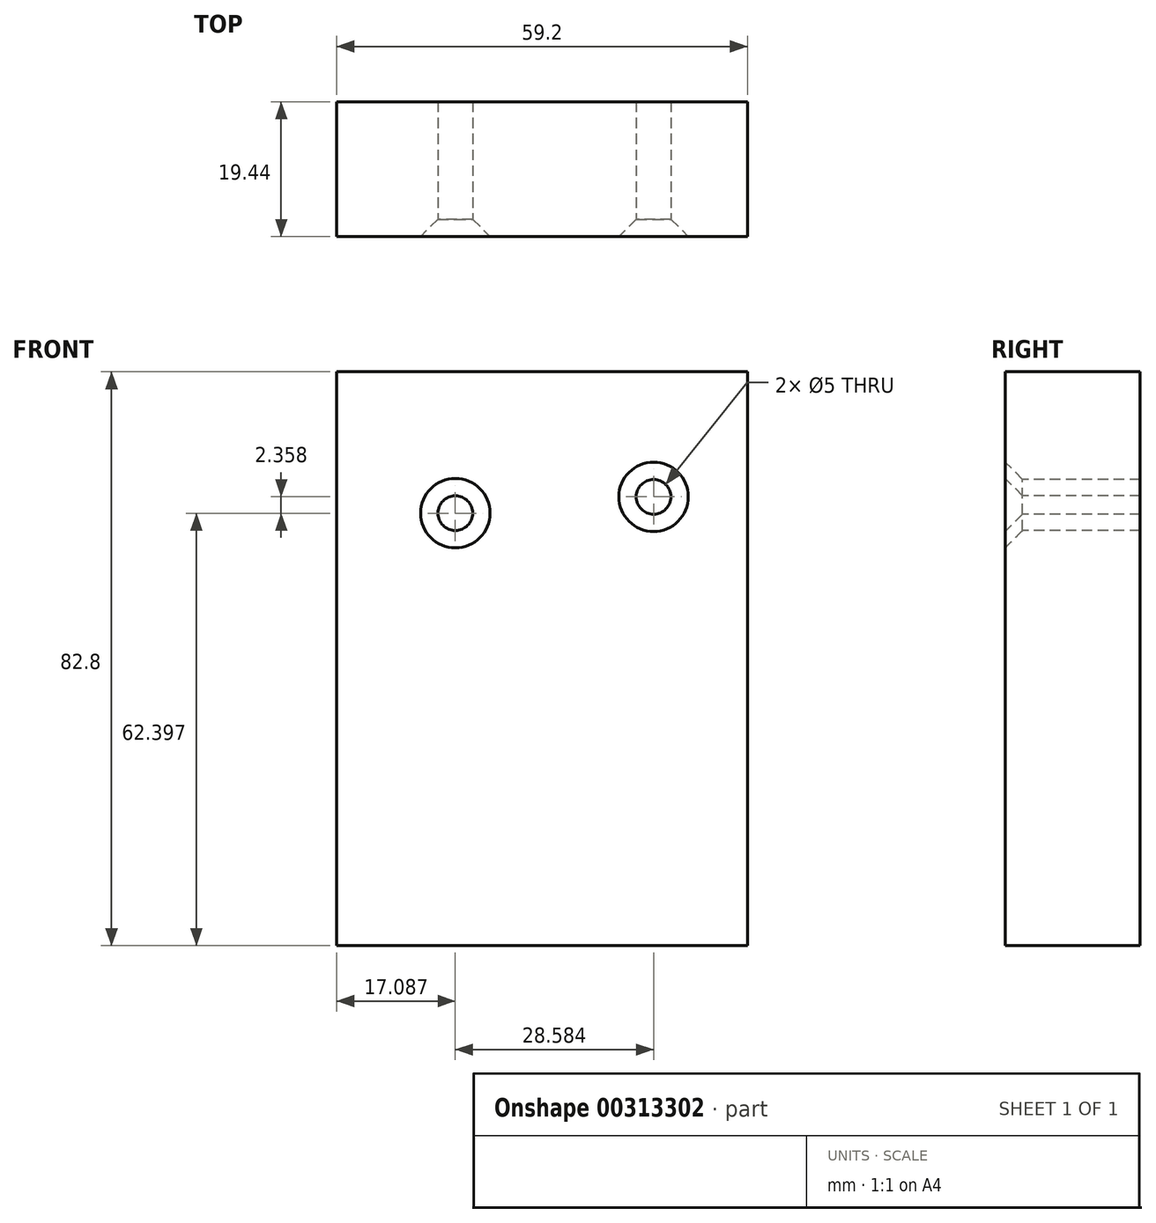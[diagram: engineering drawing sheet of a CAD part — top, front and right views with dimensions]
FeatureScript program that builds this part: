
annotation { "Feature Type Name" : "Feature", "Feature Type Description" : "" }
export const myFeature = defineFeature(function(context is Context, id is Id, definition is map)
    precondition{}
    {
        {
            var Q0;
            Q0=qCreatedBy(makeId("Top.planeOp"),FACE);
            var sketch = newSketch(context, id + "F0", { "sketchPlane" : qUnion([Q0])});
            skLineSegment(sketch, "E0.bottom", {"start": v(-35.02, -10.8) * mm, "end": v(24.18, -10.8) * mm});
            skLineSegment(sketch, "E0.top", {"start": v(-35.02, 8.65) * mm, "end": v(24.18, 8.65) * mm});
            skLineSegment(sketch, "E0.left", {"start": v(-35.02, -10.8) * mm, "end": v(-35.02, 8.65) * mm});
            skLineSegment(sketch, "E0.right", {"start": v(24.18, -10.8) * mm, "end": v(24.18, 8.65) * mm});
            skSolve(sketch);
        }
        {
            var Q0;
            Q0=makeQuery(id+"F0.imprint","IMPRINT",FACE,{"disambiguationData":[TD([[makeQuery(id+"F0.imprint","IMPRINT",EDGE,{"derivedFrom":sQuery(id+"F0.wireOp",EDGE,"E0.bottom")}),1.0]])]});
            extrude(context, id + "F1", {"entities" : qUnion([Q0]), "depth" : 82.8 * mm});
        }
        {
            var Q0;
            Q0=makeQuery(id+"F1.opExtrude","SWEPT_FACE",FACE,{"disambiguationData":[OSD([sQuery(id+"F0.wireOp",EDGE,"E0.bottom")])]});
            var sketch = newSketch(context, id + "F2", { "sketchPlane" : qUnion([Q0])});
            skPoint(sketch, "E1", {"position": v(-17.93, 62.4) * mm});
            skPoint(sketch, "E2", {"position": v(10.65, 64.75) * mm});
            skSolve(sketch);
        }
        {
            var Q0;
            Q0=sQuery(id+"F2.wireOp",VERTEX,"E1");
            var Q1;
            Q1=sQuery(id+"F2.wireOp",VERTEX,"E2");
            var Q2;
            Q2=makeQuery(id+"F1.opExtrude","SWEPT_BODY",BODY,{"disambiguationData":[OSD([sQuery(id+"F0.wireOp",EDGE,"E0.bottom"),sQuery(id+"F0.wireOp",EDGE,"E0.top"),sQuery(id+"F0.wireOp",EDGE,"E0.left"),sQuery(id+"F0.wireOp",EDGE,"E0.right")])]});
            hole(context, id + "F3", {"style" : HoleStyle.C_SINK, "endStyle" : HoleEndStyle.THROUGH, "holeDiameter" : 5 * mm, "cSinkDiameter" : 10 * mm, "cSinkAngle" : 90 * degree, "tappedDepth" : 12 * mm, "tapClearance" : 3, "locations" : qUnion([Q0, Q1]), "scope" : qUnion([Q2])});
        }
    });
